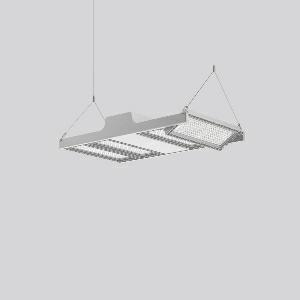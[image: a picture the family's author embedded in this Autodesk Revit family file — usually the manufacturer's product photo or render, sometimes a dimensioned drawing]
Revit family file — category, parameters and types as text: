
# Revit family: light_case_921687_004_1_76_35da
name_source: partatom
category: Lighting Fixtures
units: mm (PartAtom-declared; Revit-internal decimal feet)

## family parameters
Cut with Voids When Loaded = No
Host = Face
Light Source = No
Part Type = Normal
Room Calculation Point = No
Round Connector Dimension = Use Diameter
Shared = No

## types (1)
- LIGHT CASE (1 x LED Modul 865, 8700 lm, 6500)
    Apparent Load = 225 VA
    CIE Flux Codes = 85 97 100 100 100
    Color Rendering = 80
    Color Temperature = 6500
    Default Elevation = 1800 mm
    Description = Series: LIGHT CASE
Flat highbay luminaire for chain or cable suspension with 4 LED modules that can be swivelled. Housing: die cast aluminium and sheet steel, powder-coated. Optimised thermal management thanks to special luminaire design. Self-cleaning heat sink for constant heat dissipation. Cover: plastic (polycarbonate, shockproof), with integrated four-row lens system. LED modules can be swivelled ± 30° for optimum illumination. Suitable for chain or steel cable suspension (to be provided on site). With 5-pin connection terminal (1.5 m). With integrated movement sensor and light sensor for daylight detection on request. Ball impact proof in accordance with DIN 18032-03 (except steel cable suspension). Luminaire with limited surface temperature in accordance with EN 60598-2-24 for use in environments in which a deposit of conductive dust on the luminaire can be expected. 
Colour: silver, matt (approx. RAL 9006)
Length: 680 mm
Width: 397 mm
Height: 110 mm
Lamp: LED
Socket: without socket
Colour temperature: 6500K
Colour rendering index (CRI): 80
System power: 225 W
Rated luminous flux: 34800 lm
Luminous efficiency: 155 lm/W
Control gear: Converter, dimmable, DALI
Protection class: I
Type of protection: IP 65
    Height = 110 mm
    Lamp = 1 x LED Modul 865
    Lamp Light Flux = 8700 lm
    Lamp count = 1
    Length = 680 mm
    Lifetime = 50000 h
    Luminous efficacy = 155 lm/W
    Manufacturer = RZB
    ModVariant = No
    Model = 921687.004.1.76
    Mounting Place = Ceiling
    Mounting Type = Pendant
    Number of Poles = 1
    OnlyDefault = Yes
    Power Factor = 1
    Product Name = LIGHT CASE
    Product group = Pendant commercial luminaires
    ProductGroupID = 903
    Protection Class = Protection class I
    Protection Degree = IP 65
    RLX_Detail_Level = 1
    RLX_Emergency_Light_Flux = 0 lm
    RLX_Emergency_Type = 0
    RLX_Emergency_Type_DB = No
    RlxData = <blob elided: 29097 chars, md5=344342a3>
    Socket = socket
    Standby Power = 0 W
    System Light Flux = 34800 lm
    System Power = 225 W
    Type Comments = Product without accessories
    Type Image = 921523.004.76.jpg
    URL = http://relux.com
    VarID = ---
    Voltage = 230 V
    Voltage Range = 220-240 V
    Weight = 0.00 kg
    Width = 397 mm

## geometry (parser evidence)
native form markers: Blend x4, Sweep x21
no freeform markers — native parametric forms only
